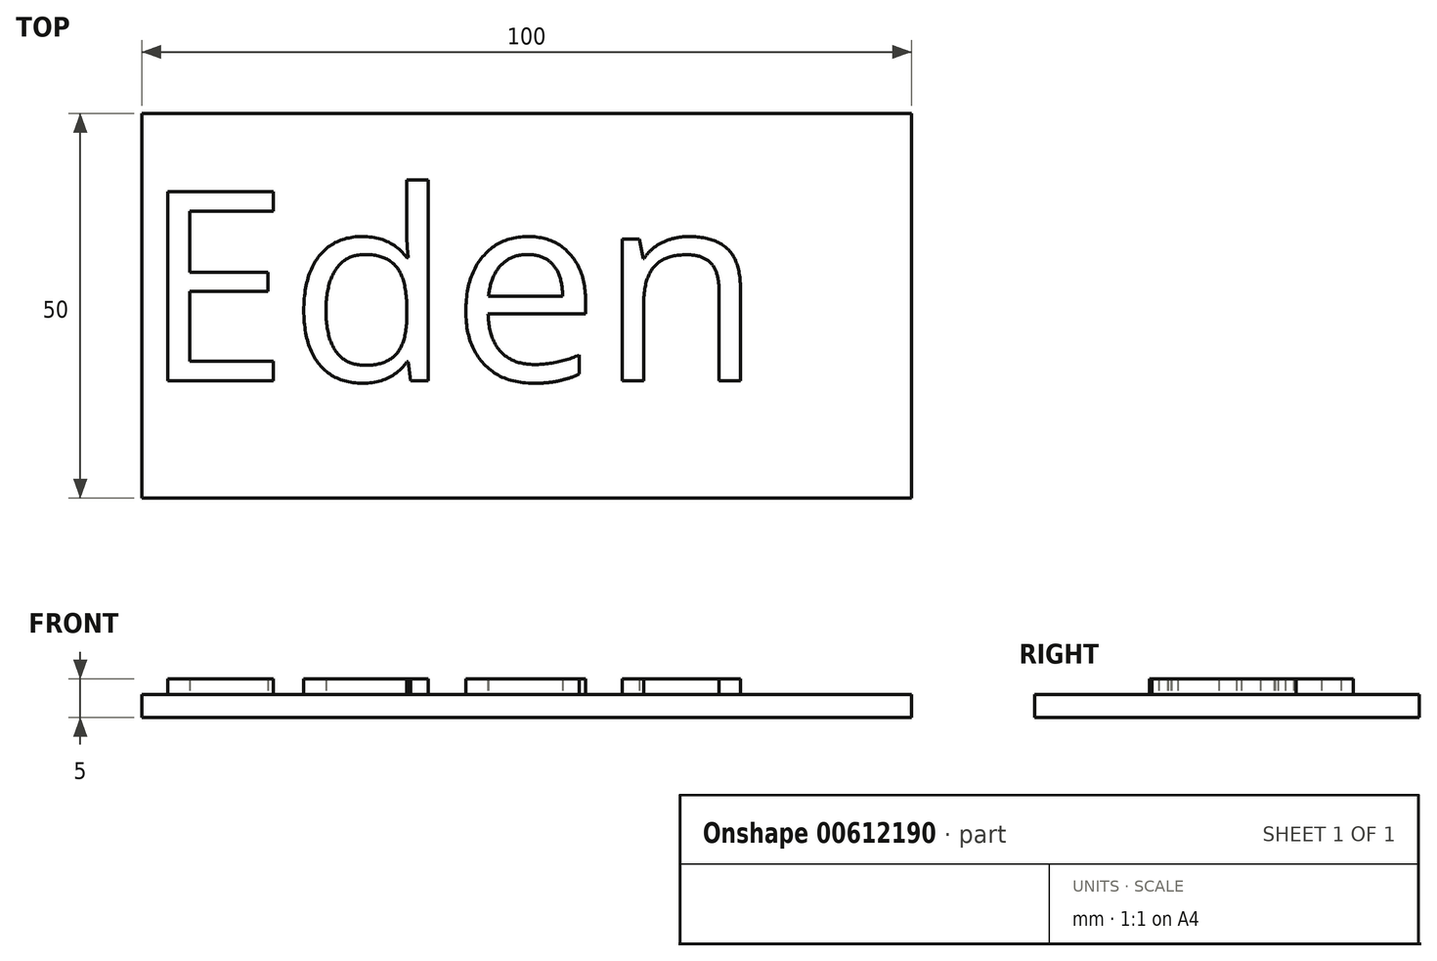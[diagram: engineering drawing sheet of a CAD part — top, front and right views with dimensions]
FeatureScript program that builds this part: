
annotation { "Feature Type Name" : "Feature", "Feature Type Description" : "" }
export const myFeature = defineFeature(function(context is Context, id is Id, definition is map)
    precondition{}
    {
        {
            var Q0;
            Q0=qCreatedBy(makeId("Top.planeOp"),FACE);
            var sketch = newSketch(context, id + "F0", { "sketchPlane" : qUnion([Q0])});
            skLineSegment(sketch, "E0.bottom", {"start": v(0, 0) * mm, "end": v(100, 0) * mm});
            skLineSegment(sketch, "E0.top", {"start": v(0, 50) * mm, "end": v(100, 50) * mm});
            skLineSegment(sketch, "E0.left", {"start": v(0, 0) * mm, "end": v(0, 50) * mm});
            skLineSegment(sketch, "E0.right", {"start": v(100, 0) * mm, "end": v(100, 50) * mm});
            skSolve(sketch);
        }
        {
            var Q0;
            Q0 = qSketchRegion(id + "F0", true);
            extrude(context, id + "F1", {"entities" : qUnion([Q0]), "depth" : 3 * mm, "offsetDistance" : 25 * mm});
        }
        {
            var Q0;
            Q0=makeQuery(id+"F1.opExtrude","CAP_FACE",FACE,{"disambiguationData":[OSD([sQuery(id+"F0.wireOp",EDGE,"E0.bottom"),sQuery(id+"F0.wireOp",EDGE,"E0.top"),sQuery(id+"F0.wireOp",EDGE,"E0.left"),sQuery(id+"F0.wireOp",EDGE,"E0.right")])],"isStart":false});
            var sketch = newSketch(context, id + "F2", { "sketchPlane" : qUnion([Q0])});
            skText(sketch, "E1", { "text": "Eden", "fontName": "OpenSans-Regular.ttf"});
            const initialGuessF2  = {"E1": [0, 0.01527, 1, 0, 0.02474]};
            skSetInitialGuess(sketch, initialGuessF2);
            skSolve(sketch);
        }
        {
            var Q0;
            Q0 = qSketchRegion(id + "F2", true);
            extrude(context, id + "F3", {"entities" : qUnion([Q0]), "operationType" : NewBodyOperationType.ADD, "depth" : 2 * mm, "offsetDistance" : 25 * mm});
        }
    });
